# Revit family: KFE 2512 11
name_source: partatom
category: Rohrzubehör
units: mm (PartAtom-declared; Revit-internal decimal feet)

## family parameters
Arbeitsebenenbasiert = Nein
Beim Laden mit Abzugskörper schneiden = Nein
Bemaßung runder Anschluss = Durchmesser verwenden
Gemeinsam genutzt = Nein
Immer vertikal = Ja
OmniClass-Nummer = 23.65.55.14
OmniClass-Titel = Valves for Liquid Services
Teiletyp = Normal

## types (1)
- KFE 2512 11
    Anwendungsgebiet = Die Entleerungshähne werden als Füll- und Entleerungshähne verwendet. Anwendungsgebiete sind in haustechnischen Anlagen, wie z.B. in Heizungs- oder Kaltwasseranlagen für die Klimatisierung von Gebäuden. Aromatische Chlorkohlenwasserstoffe wie in Erdgas oder Erdölen vorkommend, zerstören die EPDM- Dichtungen
    Betriebsdaten = Heizungswasser nach ÖNORM H5195 oder VDI- Richtlinie 2035.
Die Verwendung von Ethylen-, oder Propyleneglykol in einem Mischungsverhältnis 25- 50% ist zulässig.
    D02 = 9.3 mm  [stored 0.0305118 ft]
    D03 = 11.7 mm  [stored 0.0383858 ft]
    D04 = 11.1 mm  [stored 0.0364173 ft]
    D05 = 13.4 mm  [stored 0.0439633 ft]
    D06 = 12.1 mm
    D07 = 14.5 mm  [stored 0.0475722 ft]
    D08 = 7 mm  [stored 0.0229659 ft]
    Dichtungen = Kugel: PTFE, Spindel: PTFE
    G02 = 13.2 mm  [stored 0.0433071 ft]
    Gehäuse = geschmiedetes Messing CW617N
    H00 = 17 mm
    Hersteller = Herz-Armaturen GmbH
    Kugel = geschmiedetes CW617N, volle Bohrung, Oberfläche verchromt
    L00 = 44 mm  [stored 0.144357 ft]
    L01 = 19.5 mm  [stored 0.0639764 ft]
    L02 = 13 mm
    L03 = 8.5 mm  [stored 0.0278871 ft]
    L04 = 9.5 mm  [stored 0.031168 ft]
    L05 = 6.5 mm
    L06 = 19 mm  [stored 0.062336 ft]
    L07 = 4 mm  [stored 0.0131234 ft]
    L08 = 8 mm  [stored 0.0262467 ft]
    L09 = 13.5 mm  [stored 0.0442913 ft]
    L10 = 14 mm  [stored 0.0459318 ft]
    R01 = 7 mm  [stored 0.0229659 ft]
    R99 = 2 mm  [stored 0.00656168 ft]
    S01 = 51 mm  [stored 0.167323 ft]
    S02 = 24.5 mm
    S03 = 16 mm  [stored 0.0524934 ft]
    S04 = 45 mm  [stored 0.147638 ft]
    SCRNCODE = 05;08;01
    SCRNSEQ = ARM;ARM_TYP="ABSV";1
    SCTWCODE = 01;10;01
    SCTWSEQ = ENT;AO;1
    Spindel = Messing CW614N
    URL = www.herz-armaturen.at
    Vorgabe-Ansicht = 0 mm  [stored 0 ft]
    max.Betriebsdruck = 1000000.0 Pa
    max.Betriebstemperatur = 110 °C
    min.Betriebstemperatur = -30 °C

note: [stored X ft] marks values corroborated as IEEE doubles in the binary element streams (Revit-internal decimal feet)
